# Revit family: HBLH
name_source: partatom
category: Lighting Fixtures
units: mm (PartAtom-declared; Revit-internal decimal feet)

## family parameters
Cut with Voids When Loaded = No
Host = Face
Light Source = Yes
OmniClass Number = 23.80.70.14.14
OmniClass Title = Exterior Floodlights
Part Type = Normal
Room Calculation Point = No
Round Connector Dimension = Use Diameter
Shared = No

## types (1)
- HBLH
    Apparent Load = 57 VA
    Certification = CSA Listed to UL844
• CSA Listed to UL1598 Wet Location
• Wet Location listed up to 90 degrees
• Damp location listed at greater than 90 degrees mounting angle
• Class I, Division 2, Groups A, B, C & D
• IP66 with factory installed ENCG option
    Color Filter = 16777215
    Default Elevation = 48 "
    Description = The HBLH Series Hazardous LED Flood Light is designed to efficiently light classified areas in heavy industrial settings.
    Dimming Lamp Color Temperature Shift = <None>
    Emit Shape Visible in Rendering = No
    Emit from Circle Diameter = 11 "
    Fastners = Paint - Light Silver
    Glass = Glass
    Lamp = 24 High Performanc LEDs
    Load Classification = Lighting
    Manufacturer = Columbia Lighting
    Material Finish = Paint -  White Texture
    Model = HBLH
    Optics = Narrow
    Photometric Web File = HBLH60LU5KA070WH.ies
    Power Factor = 1
    Tilt Angle = -90.00°
    URL = https://www.currentlighting.com
    Voltage = 277 V
    Warranty = 5 Year Warranty
    Watt = 57 W
    Wattage Comments = 57 Watts, 24 LEDs

## geometry (parser evidence)
native form markers: Blend x4, Sweep x4
no freeform markers — native parametric forms only
